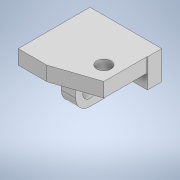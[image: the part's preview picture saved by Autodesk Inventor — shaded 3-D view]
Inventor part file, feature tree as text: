
AUTODESK INVENTOR PART (.ipt)
format: ipt  version: 2020 (Build 240168000, 168)  size: 148,992 bytes
history: native  units: mm
features: extrude x5, sketch x5, other x1, fillet x1
ambient origin geometry x8: Origin, YZ Plane, XZ Plane, XY Plane, X Axis, Y Axis, Z Axis, Center Point
bodies: Body1 (feature_tree)
feature tree (12):
  other  "實體1"
  extrude  "擠出1"  Depth=50.0mm
  extrude  "擠出2"  Depth=20.0mm
  extrude  "擠出3"  Depth=10.0mm TaperAngle=0.0deg
  fillet  "圓角1"  Radius=10.0mm
  extrude  "擠出4"  Depth=10.0mm
  extrude  "擠出5"  Depth=40.0mm
  sketch  "草圖1"
  sketch  "草圖2"
  sketch  "草圖3"
  sketch  "草圖4"
  sketch  "草圖5"
